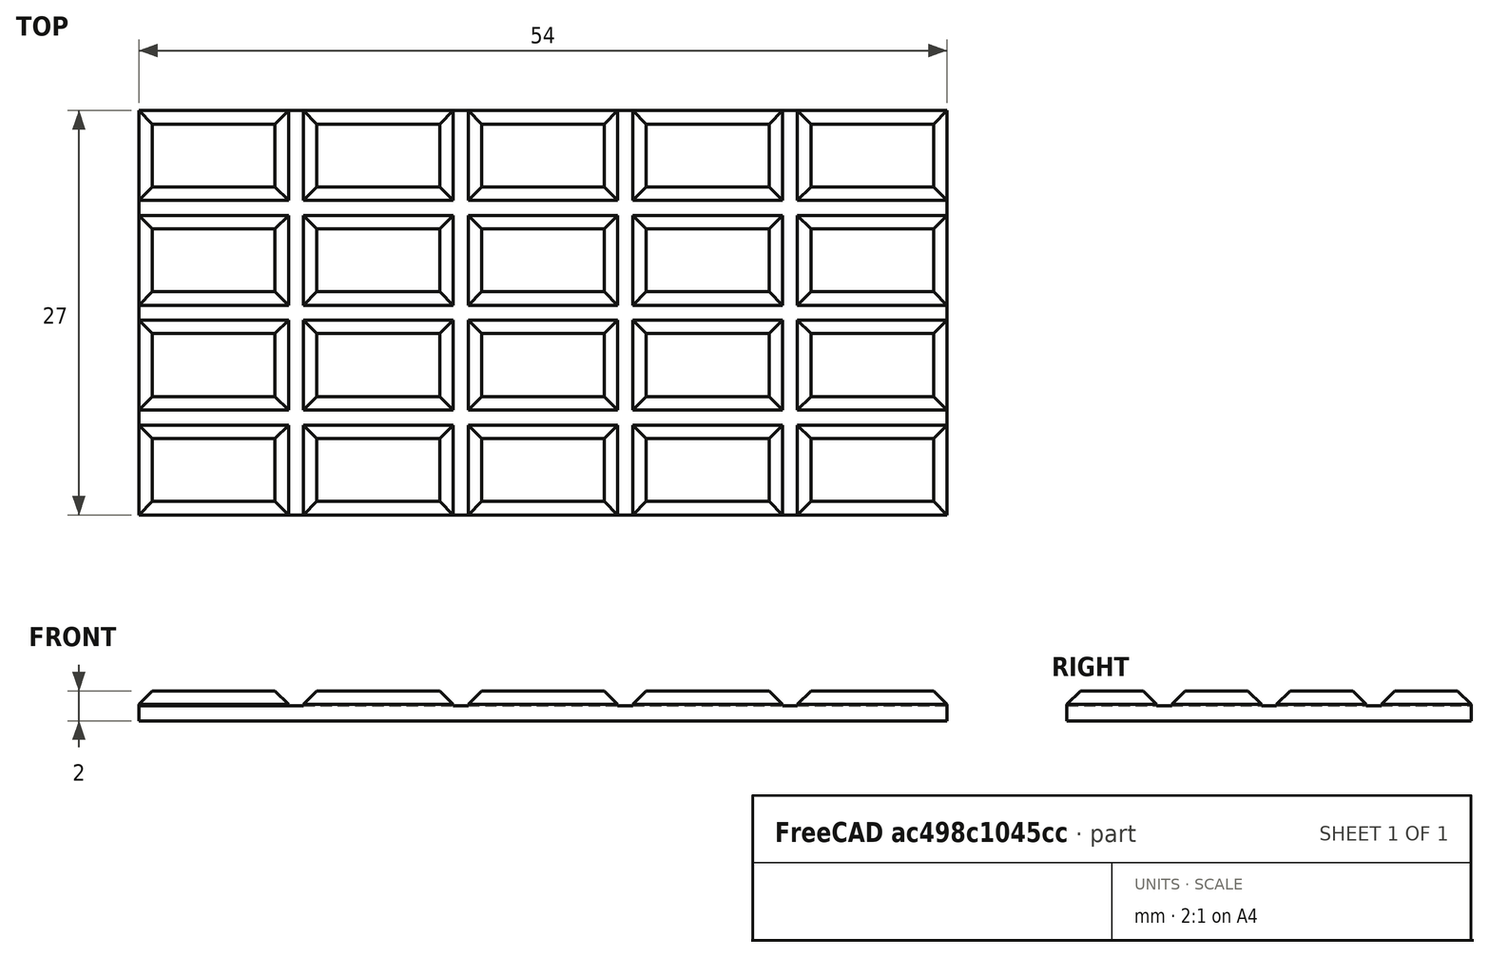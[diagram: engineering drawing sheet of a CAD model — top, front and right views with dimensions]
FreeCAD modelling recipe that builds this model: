
FCSTD DOCUMENT  (FreeCAD 1.0R39319 (Git))
Label: ojt1_t12r02_chocolat
License: All rights reserved
LicenseURL: https://en.wikipedia.org/wiki/All_rights_reserved
objects: Part::Box×2, Part::Chamfer×1, Part::FeaturePython×1, Part::MultiFuse×1
note: 4 computed .brp shape members not serialized (recipe doc carries the construction recipe); baked Part::Feature solids carry a one-line shape summary decoded from their .brp

FEATURE [Part::Box] Box  label="Cub"
  AttacherType = Attacher::AttachEngine3D
  Height = 1
  Length = 54
  Width = 27
FEATURE [Part::Box] Box001  label="Cub001"
  AttacherType = Attacher::AttachEngine3D
  Height = 1
  Length = 10
  Placement = pos=(0,0,1) rot=(0,0,1;0rad)
  Width = 6
FEATURE [Part::Chamfer] Chamfer
  Base = -> Box001
  EdgeLinks = -> Box001 [Edge2,Edge6,Edge10,Edge12]
  Edges = 4 edges r=0.9: [Edge2,Edge6,Edge10,Edge12]
FEATURE [Part::FeaturePython] Array  # Draft array (typed FeaturePython)
  AlwaysSyncPlacement = false
  Angle = 360
  ArrayType = 0
  Axis = (0,0,1)
  Base = -> Chamfer
  Center = (0,0,0)
  Count = 20
  ExpandArray = false
  Fuse = false
  IntervalAxis = (0,0,0)
  IntervalX = (11,0,0)
  IntervalY = (0,7,0)
  IntervalZ = (0,0,100)
  NumberCircles = 3
  NumberPolar = 5
  NumberX = 5
  NumberY = 4
  NumberZ = 1
  PlacementList = 20 placements: [(0,0,0),(0,7,0),(0,14,0),(0,21,0),(11,0,0),(11,7,0),(11,14,0),(11,21,0),(22,0,0),(22,7,0),(22,14,0),(22,21,0),(33,0,0),(33,7,0),(33,14,0),(33,21,0),(44,0,0),(44,7,0),(44,14,0),(44,21,0)]
  RadialDistance = 50
  ScaleList = (20) [(1,1,1),(1,1,1),(1,1,1),(1,1,1),(1,1,1),(1,1,1),(1,1,1),(1,1,1),(1,1,1),(1,1,1),(1,1,1),(1,1,1),(1,1,1),(1,1,1),(1,1,1),(1,1,1),(1,1,1),(1,1,1),(1,1,1),(1,1,1)]
  Symmetry = 1
  TangentialDistance = 25
FEATURE [Part::MultiFuse] Fusion
  Refine = true
  Shapes = -> [Box,Array]
